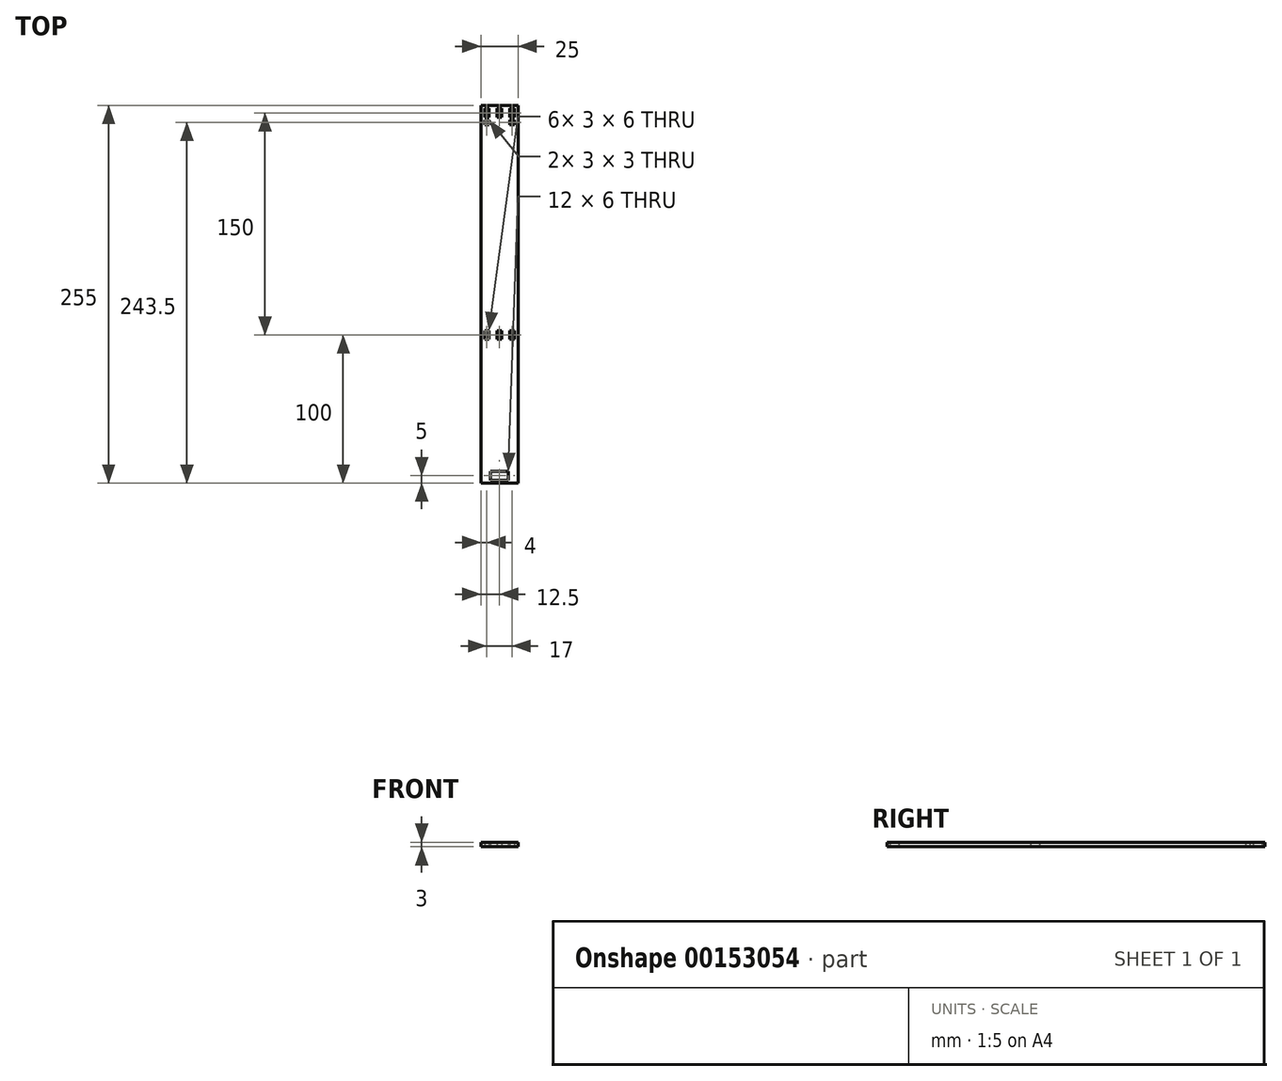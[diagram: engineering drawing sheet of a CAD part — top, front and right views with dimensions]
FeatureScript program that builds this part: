
annotation { "Feature Type Name" : "Feature", "Feature Type Description" : "" }
export const myFeature = defineFeature(function(context is Context, id is Id, definition is map)
    precondition{}
    {
        {
            var Q0;
            Q0=qCreatedBy(makeId("Top.planeOp"),FACE);
            var sketch = newSketch(context, id + "F0", { "sketchPlane" : qUnion([Q0])});
            skLineSegment(sketch, "E0", {"start": v(-12.5, 0) * mm, "end": v(-12.5, -98) * mm});
            skLineSegment(sketch, "E1", {"start": v(12.5, -98) * mm, "end": v(12.5, 0) * mm});
            skLineSegment(sketch, "E2", {"start": v(0, 0) * mm, "end": v(0, -98) * mm, "construction": true});
            skLineSegment(sketch, "E3", {"start": v(-12.5, 0) * mm, "end": v(-12.5, 7) * mm});
            skLineSegment(sketch, "E4", {"start": v(12.5, 7) * mm, "end": v(12.5, 0) * mm});
            skLineSegment(sketch, "E5", {"start": v(0, 7) * mm, "end": v(0, 5) * mm, "construction": true});
            skPoint(sketch, "E5.endSnap0", {"position": v(0, 7) * mm});
            skLineSegment(sketch, "E6", {"start": v(0, 5) * mm, "end": v(-10, 5) * mm, "construction": true});
            skLineSegment(sketch, "E7", {"start": v(-10, 5) * mm, "end": v(10, 5) * mm, "construction": true});
            skLineSegment(sketch, "E8.bottom", {"start": v(-10, 5) * mm, "end": v(-7, 5) * mm});
            skLineSegment(sketch, "E8.top", {"start": v(-10, -1) * mm, "end": v(-7, -1) * mm});
            skLineSegment(sketch, "E8.left", {"start": v(-10, 5) * mm, "end": v(-10, -1) * mm});
            skLineSegment(sketch, "E8.right", {"start": v(-7, 5) * mm, "end": v(-7, -1) * mm});
            skLineSegment(sketch, "E9", {"start": v(-7, 5) * mm, "end": v(-1.5, 5) * mm, "construction": true});
            skLineSegment(sketch, "E10.bottom", {"start": v(-1.5, 5) * mm, "end": v(1.5, 5) * mm});
            skLineSegment(sketch, "E10.top", {"start": v(-1.5, -1) * mm, "end": v(1.5, -1) * mm});
            skLineSegment(sketch, "E10.left", {"start": v(-1.5, 5) * mm, "end": v(-1.5, -1) * mm});
            skLineSegment(sketch, "E10.right", {"start": v(1.5, 5) * mm, "end": v(1.5, -1) * mm});
            skLineSegment(sketch, "E11.bottom", {"start": v(10, 5) * mm, "end": v(7, 5) * mm});
            skLineSegment(sketch, "E11.top", {"start": v(10, -1) * mm, "end": v(7, -1) * mm});
            skLineSegment(sketch, "E11.left", {"start": v(10, 5) * mm, "end": v(10, -1) * mm});
            skLineSegment(sketch, "E11.right", {"start": v(7, 5) * mm, "end": v(7, -1) * mm});
            skLineSegment(sketch, "E12", {"start": v(10, -1) * mm, "end": v(10, 157) * mm, "construction": true});
            skLineSegment(sketch, "E13", {"start": v(10, 157) * mm, "end": v(10, 155) * mm, "construction": true});
            skLineSegment(sketch, "E14.bottom", {"start": v(10, 155) * mm, "end": v(7, 155) * mm});
            skLineSegment(sketch, "E14.top", {"start": v(10, 149) * mm, "end": v(7, 149) * mm});
            skLineSegment(sketch, "E14.left", {"start": v(10, 155) * mm, "end": v(10, 149) * mm});
            skLineSegment(sketch, "E14.right", {"start": v(7, 155) * mm, "end": v(7, 149) * mm});
            skLineSegment(sketch, "E15", {"start": v(7, 155) * mm, "end": v(1.5, 155) * mm, "construction": true});
            skLineSegment(sketch, "E16.bottom", {"start": v(1.5, 155) * mm, "end": v(-1.5, 155) * mm});
            skLineSegment(sketch, "E16.top", {"start": v(1.5, 149) * mm, "end": v(-1.5, 149) * mm});
            skLineSegment(sketch, "E16.left", {"start": v(1.5, 155) * mm, "end": v(1.5, 149) * mm});
            skLineSegment(sketch, "E16.right", {"start": v(-1.5, 155) * mm, "end": v(-1.5, 149) * mm});
            skLineSegment(sketch, "E17", {"start": v(-1.5, 155) * mm, "end": v(-7, 155) * mm, "construction": true});
            skLineSegment(sketch, "E18.bottom", {"start": v(-7, 155) * mm, "end": v(-10, 155) * mm});
            skLineSegment(sketch, "E18.top", {"start": v(-7, 149) * mm, "end": v(-10, 149) * mm});
            skLineSegment(sketch, "E18.left", {"start": v(-7, 155) * mm, "end": v(-7, 149) * mm});
            skLineSegment(sketch, "E18.right", {"start": v(-10, 155) * mm, "end": v(-10, 149) * mm});
            skLineSegment(sketch, "E19", {"start": v(-12.5, 7) * mm, "end": v(-12.5, 157) * mm});
            skLineSegment(sketch, "E20", {"start": v(-12.5, 157) * mm, "end": v(10, 157) * mm});
            skLineSegment(sketch, "E21", {"start": v(12.5, 7) * mm, "end": v(12.5, 157) * mm});
            skLineSegment(sketch, "E22", {"start": v(12.5, 157) * mm, "end": v(10, 157) * mm});
            skLineSegment(sketch, "E23", {"start": v(0, 149) * mm, "end": v(0, 147) * mm, "construction": true});
            skLineSegment(sketch, "E24", {"start": v(0, 147) * mm, "end": v(-10, 147) * mm, "construction": true});
            skLineSegment(sketch, "E25", {"start": v(-10, 147) * mm, "end": v(10, 147) * mm, "construction": true});
            skLineSegment(sketch, "E26.bottom", {"start": v(-10, 147) * mm, "end": v(-7, 147) * mm});
            skLineSegment(sketch, "E26.top", {"start": v(-10, 144) * mm, "end": v(-7, 144) * mm});
            skLineSegment(sketch, "E26.left", {"start": v(-10, 147) * mm, "end": v(-10, 144) * mm});
            skLineSegment(sketch, "E26.right", {"start": v(-7, 147) * mm, "end": v(-7, 144) * mm});
            skLineSegment(sketch, "E27.bottom", {"start": v(10, 147) * mm, "end": v(7, 147) * mm});
            skLineSegment(sketch, "E27.top", {"start": v(10, 144) * mm, "end": v(7, 144) * mm});
            skLineSegment(sketch, "E27.left", {"start": v(10, 147) * mm, "end": v(10, 144) * mm});
            skLineSegment(sketch, "E27.right", {"start": v(7, 147) * mm, "end": v(7, 144) * mm});
            skLineSegment(sketch, "E28", {"start": v(0, -90) * mm, "end": v(6, -90) * mm, "construction": true});
            skLineSegment(sketch, "E29", {"start": v(6, -90) * mm, "end": v(-6, -90) * mm, "construction": true});
            skLineSegment(sketch, "E30", {"start": v(-6, -90) * mm, "end": v(-6, -96) * mm, "construction": true});
            skLineSegment(sketch, "E31", {"start": v(-6, -96) * mm, "end": v(6, -96) * mm, "construction": true});
            skLineSegment(sketch, "E32", {"start": v(6, -96) * mm, "end": v(6, -90) * mm, "construction": true});
            skLineSegment(sketch, "E33.bottom", {"start": v(-6, -90) * mm, "end": v(6, -90) * mm, "construction": true});
            skLineSegment(sketch, "E33.right", {"start": v(6, -90) * mm, "end": v(6, -96) * mm, "construction": true});
            skLineSegment(sketch, "E34.bottom", {"start": v(-6, -90) * mm, "end": v(6, -90) * mm});
            skLineSegment(sketch, "E34.top", {"start": v(-6, -96) * mm, "end": v(6, -96) * mm});
            skLineSegment(sketch, "E34.left", {"start": v(-6, -90) * mm, "end": v(-6, -96) * mm});
            skLineSegment(sketch, "E34.right", {"start": v(6, -90) * mm, "end": v(6, -96) * mm});
            skLineSegment(sketch, "E35", {"start": v(-12.5, -98) * mm, "end": v(12.5, -98) * mm});
            skLineSegment(sketch, "E36.trimOffspring", {"start": v(0, -98) * mm, "end": v(0, -90) * mm, "construction": true});
            skSolve(sketch);
        }
        {
            var Q0;
            Q0=makeQuery(id+"F0.imprint","IMPRINT",FACE,{"disambiguationData":[TD([[makeQuery(id+"F0.imprint","IMPRINT",EDGE,{"derivedFrom":sQuery(id+"F0.wireOp",EDGE,"E0")}),1.0]])]});
            extrude(context, id + "F1", {"entities" : qUnion([Q0]), "endBound" : BoundingType.SYMMETRIC, "depth" : 3 * mm});
        }
    });
